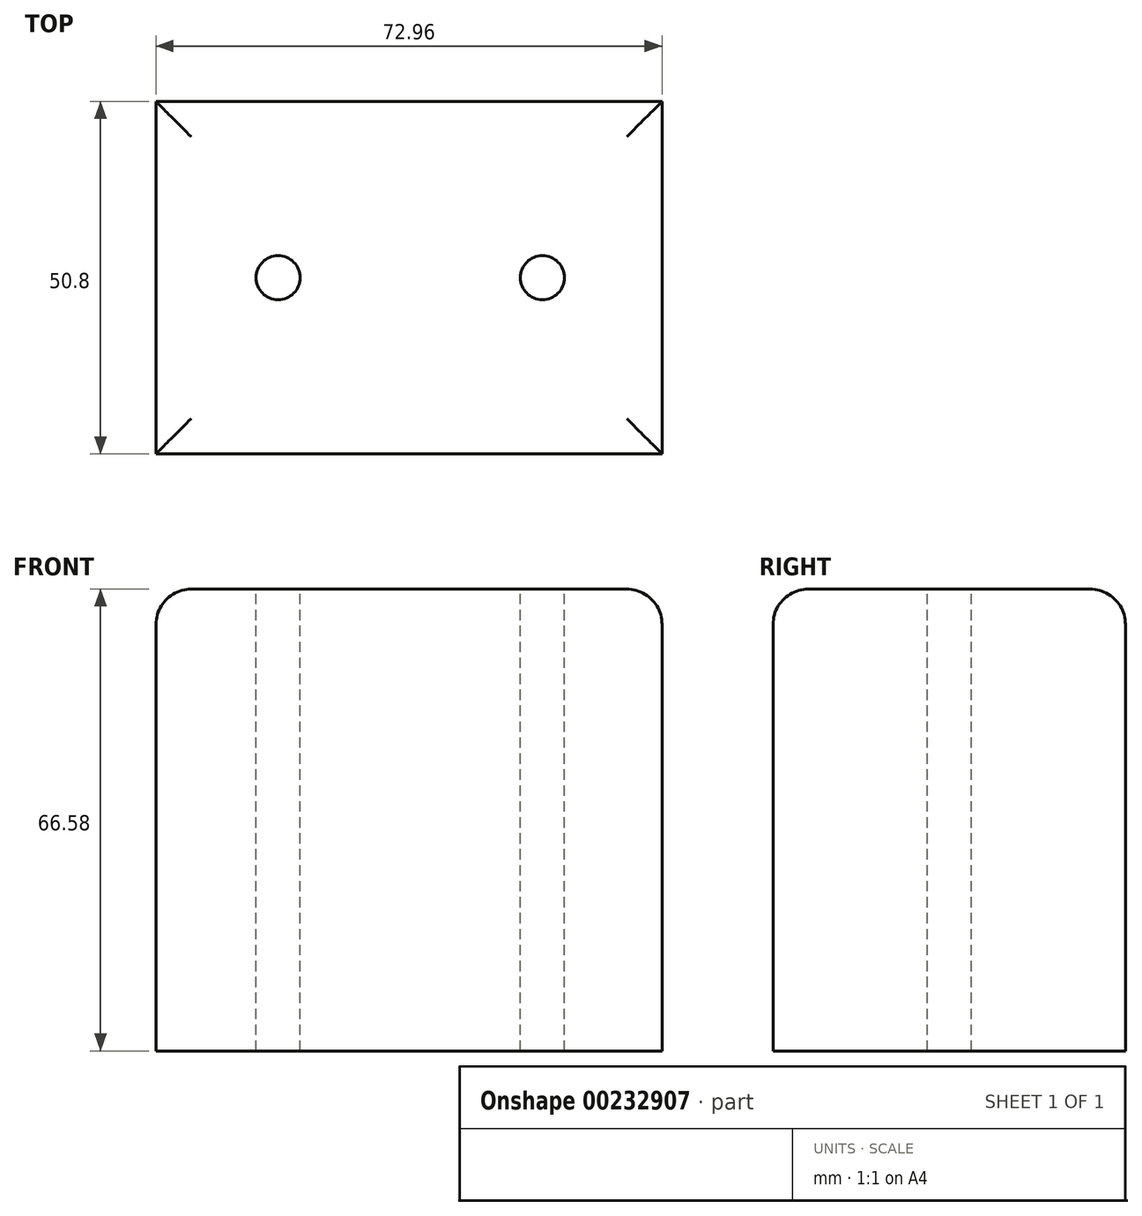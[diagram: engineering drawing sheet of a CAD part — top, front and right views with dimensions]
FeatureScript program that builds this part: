
annotation { "Feature Type Name" : "Feature", "Feature Type Description" : "" }
export const myFeature = defineFeature(function(context is Context, id is Id, definition is map)
    precondition{}
    {
        {
            var Q0;
            Q0=qCreatedBy(makeId("Front.planeOp"),FACE);
            var sketch = newSketch(context, id + "F0", { "sketchPlane" : qUnion([Q0])});
            skLineSegment(sketch, "E0.bottom", {"start": v(-36.48, 33.3) * mm, "end": v(36.48, 33.3) * mm});
            skLineSegment(sketch, "E0.top", {"start": v(-36.48, -33.3) * mm, "end": v(36.48, -33.3) * mm});
            skLineSegment(sketch, "E0.left", {"start": v(-36.48, 33.3) * mm, "end": v(-36.48, -33.3) * mm});
            skLineSegment(sketch, "E0.right", {"start": v(36.48, 33.3) * mm, "end": v(36.48, -33.3) * mm});
            skPoint(sketch, "E0.middle", {"position": v(0, 0) * mm});
            skSolve(sketch);
        }
        {
            var Q0;
            Q0=makeQuery(id+"F0.imprint","IMPRINT",FACE,{"disambiguationData":[TD([[makeQuery(id+"F0.imprint","IMPRINT",EDGE,{"derivedFrom":sQuery(id+"F0.wireOp",EDGE,"E0.bottom")}),-1.0]])]});
            extrude(context, id + "F1", {"entities" : qUnion([Q0]), "depth" : 50.8 * mm});
        }
        {
            var Q0;
            Q0=makeQuery(id+"F1.opExtrude","SWEPT_EDGE",EDGE,{"disambiguationData":[OSD([sQuery(id+"F0.wireOp",EDGE,"E0.bottom"),sQuery(id+"F0.wireOp",EDGE,"E0.right")])]});
            var Q1;
            Q1=makeQuery(id+"F1.opExtrude","CAP_EDGE",EDGE,{"disambiguationData":[OSD([sQuery(id+"F0.wireOp",EDGE,"E0.bottom")])],"isStart":false});
            var Q2;
            Q2=makeQuery(id+"F1.opExtrude","SWEPT_EDGE",EDGE,{"disambiguationData":[OSD([sQuery(id+"F0.wireOp",EDGE,"E0.bottom"),sQuery(id+"F0.wireOp",EDGE,"E0.left")])]});
            var Q3;
            Q3=makeQuery(id+"F1.opExtrude","CAP_EDGE",EDGE,{"disambiguationData":[OSD([sQuery(id+"F0.wireOp",EDGE,"E0.bottom")])],"isStart":true});
            fillet(context, id + "F2", {"entities" : qUnion([Q0, Q1, Q2, Q3]), "radius" : 5.08 * mm, "tangentPropagation" : true, "allowEdgeOverflow" : false});
        }
        {
            var Q0;
            Q0=makeQuery(id+"F1.opExtrude","SWEPT_FACE",FACE,{"disambiguationData":[OSD([sQuery(id+"F0.wireOp",EDGE,"E0.bottom")])]});
            var sketch = newSketch(context, id + "F3", { "sketchPlane" : qUnion([Q0])});
            skPoint(sketch, "E1", {"position": v(-18.87, -25.4) * mm});
            skPoint(sketch, "E2", {"position": v(19.23, -25.4) * mm});
            skSolve(sketch);
        }
        {
            var Q0;
            Q0=sQuery(id+"F3.wireOp",VERTEX,"E1");
            var Q1;
            Q1=sQuery(id+"F3.wireOp",VERTEX,"E2");
            var Q2;
            Q2=makeQuery(id+"F1.opExtrude","SWEPT_BODY",BODY,{"disambiguationData":[OSD([sQuery(id+"F0.wireOp",EDGE,"E0.bottom"),sQuery(id+"F0.wireOp",EDGE,"E0.top"),sQuery(id+"F0.wireOp",EDGE,"E0.left"),sQuery(id+"F0.wireOp",EDGE,"E0.right")])]});
            hole(context, id + "F4", {"style" : HoleStyle.SIMPLE, "endStyle" : HoleEndStyle.THROUGH, "holeDiameter" : 6.35 * mm, "locations" : qUnion([Q0, Q1]), "scope" : qUnion([Q2]), "isTappedThrough" : true});
        }
    });
